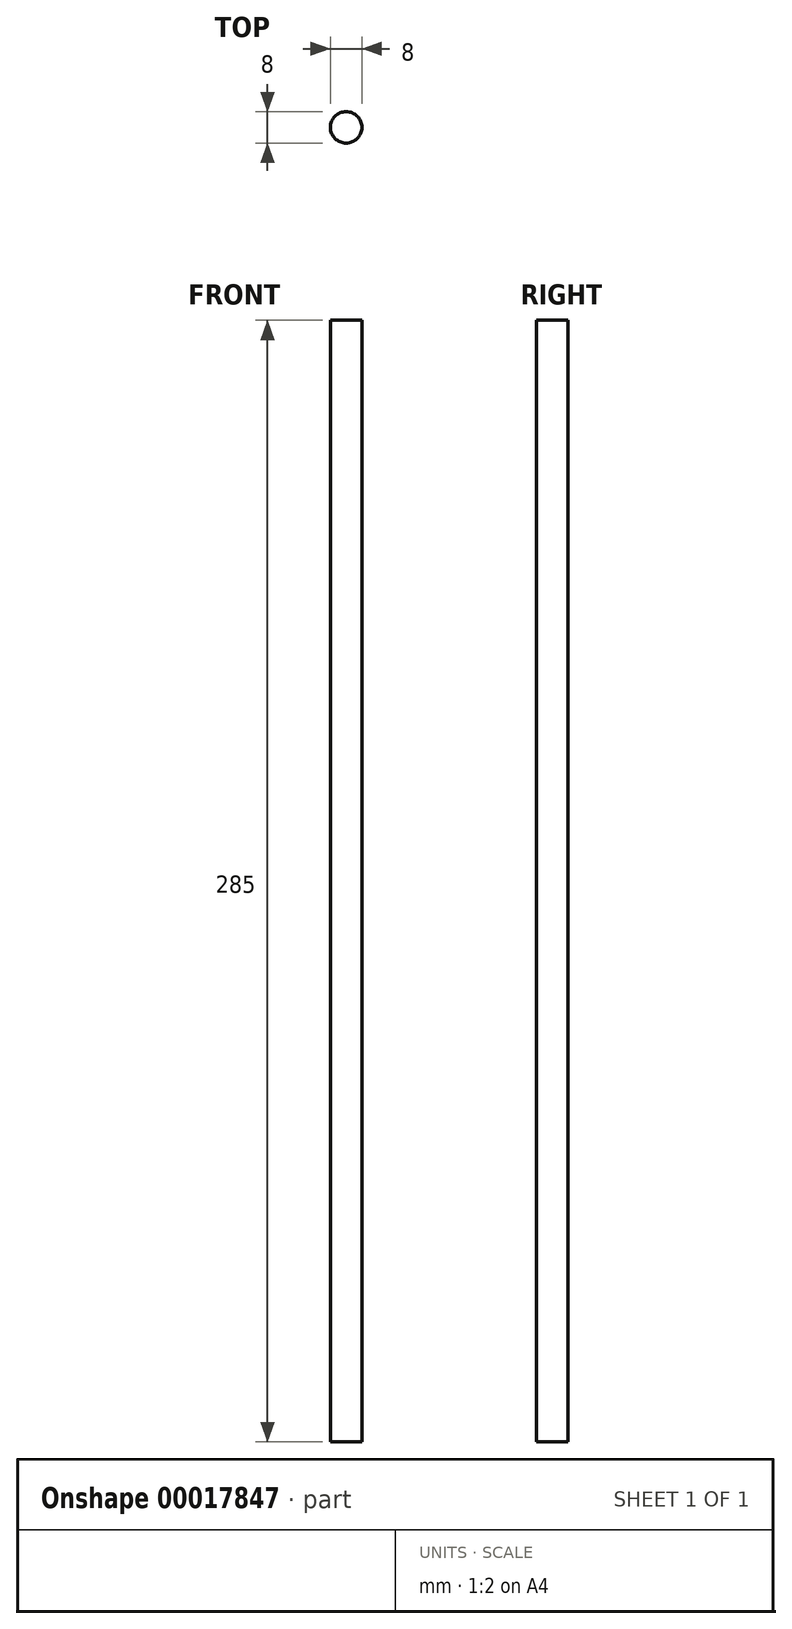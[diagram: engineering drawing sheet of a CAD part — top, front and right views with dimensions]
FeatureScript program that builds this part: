
annotation { "Feature Type Name" : "Feature", "Feature Type Description" : "" }
export const myFeature = defineFeature(function(context is Context, id is Id, definition is map)
    precondition{}
    {
        {
            var Q0;
            Q0=qCreatedBy(makeId("Top.planeOp"),FACE);
            var sketch = newSketch(context, id + "F0", { "sketchPlane" : qUnion([Q0])});
            skCircle(sketch, "E0", {"center": v(0, 0) * mm, "radius": 4 * mm});
            skSolve(sketch);
        }
        {
            var Q0;
            Q0=qSketchRegion(id+"F0",true);
            extrude(context, id + "F1", {"entities" : qUnion([Q0]), "depth" : 285 * mm});
        }
    });
